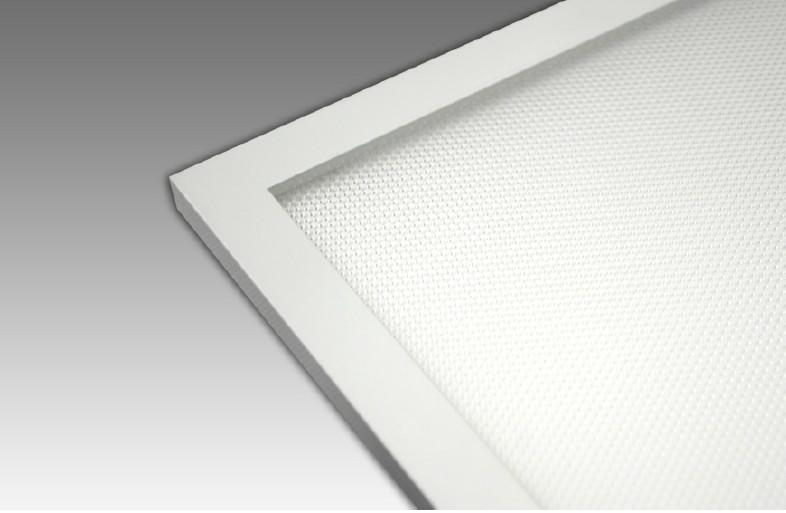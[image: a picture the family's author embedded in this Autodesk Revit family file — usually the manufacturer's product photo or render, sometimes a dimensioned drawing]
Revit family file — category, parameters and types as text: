
# Revit family: DG1012MON
name_source: partatom
category: Lighting Fixtures
revit_build: Autodesk Revit 2017 (Build: 20160225_1515(x64)
units: mm (PartAtom-declared; Revit-internal decimal feet)

## family parameters
Cut with Voids When Loaded = No
Host = Face
Light Source = Yes
Part Type = Normal
Room Calculation Point = No
Round Connector Dimension = Use Diameter
Shared = No

## types (4) — shared parameters
Color Filter = 16777215
Default Elevation = 1219 mm
Dimming Lamp Color Temperature Shift = <None>
Emit Shape Visible in Rendering = Yes
Emit from Circle Diameter = 79 mm
Lamp = LED
Manufacturer = ARLIGHT
Model = DG1012MON
Tilt Angle = 90.00°
Type Comments = DOWNLIGHT
Type Image = <None>

## per-type parameters (varying)
| type | Apparent Load | Photometric Web File | Wattage Comments |
| DGMON.120.7.30 | 7 VA | dg-1012-mow-7w-3k-sg.ies | 7 |
| DGMON.120.7.40 | 7 VA | dg-1012-mow-7w-4k-sg.ies | 7 |
| DGMON.120.10.30 | 10 VA | dg-1012-mow-10w-3k-sg.ies | 10 |
| DGMON.120.10.40 | 10 VA | dg-1012-mow-10w-4k-sg.ies | 10 |

## geometry (parser evidence)
native form markers: Sweep x3
no freeform markers — native parametric forms only
